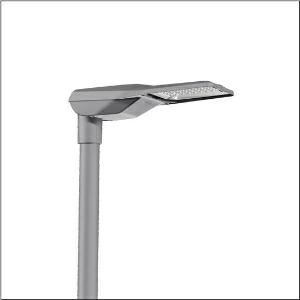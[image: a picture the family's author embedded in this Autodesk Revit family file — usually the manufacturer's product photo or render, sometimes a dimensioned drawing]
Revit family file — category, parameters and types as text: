
# Revit family: streetlight_sl_21_iq_mini___st0_8a_5xe2c41d08jb_a90a
name_source: partatom
category: Lighting Fixtures
units: mm (PartAtom-declared; Revit-internal decimal feet)

## family parameters
Cut with Voids When Loaded = No
Host = Face
Light Source = No
Part Type = Normal
Room Calculation Point = No
Round Connector Dimension = Use Diameter
Shared = No

## types (1)
- --- (1 x LED, 11290 lm, 71.6 W, 4000K)
    Apparent Load = 72 VA
    CIE Flux Codes = 41 75 97 100 100
    Color Rendering = 70
    Color Temperature = 4000K
    Default Elevation = 1800 mm
    Description = Streetlight SL 21 iQ mini, mast luminaire, primary light control with lens, of PMMA, primary optical cover: cover, of toughened safety glass, transparent, light distribution: ST0.8a, light emission: direct distribution, primary light characteristic: asymmetric, installation type: post-top, side-entry, LED, High Power LED, rated luminous flux: 11.290lm, luminous efficacy: 158lm/W, light colour: 740, colour temperature: 4000K, control: Auto-Match, Temp-Guard, Lumen-Switch, Night-Set, Smart-Wire, Light-Fading, Desk-Remote (wireless, voltage-free reading and setting of iQ features in the workshop via application-optimized NFC function/RFID function), optimised constant luminous flux control (CLO 2.0), presetting dimming linear, mains connection: 220..240V, AC, 50/60Hz, start of lifetime: 72W, end of service life: 75W, reduction: 33W, luminaire housing, of diecast aluminium, powder-coated, Siteco® metallic grey (DB 702S), corrosivity category C5 mid according to DIN EN ISO 12944, please order mast flange separately, inclination adjustable: 0°, 5°, 10°, 15°, sealing non-destructively replaceable, multi-level sealing system, length: 628mm, width: 235mm, height: 110mm, mast flange for spigot size: 42mm (side-entry): 5XC10008XM4, 60/48mm (side-entry/post-top): 5XC10108XM2, 76/60mm (side-entry/post-top): 5XC10108XM1, protection rating (complete): IP66, insulation class (complete): insulation class II (safety insulation), certification: CE, ENEC, ENEC+, VDE, impact resistance: IK09, permissible operating ambient temperature for outdoor applications: -40..+50°C, standard-compliant lighting for roads and squares, packaging unit: 1 piece

Light Distribution: ST0.8a
    Height = 110 mm
    Lamp = 1 x LED
    Lamp Light Flux = 11290 lm
    Lamp Power = 71.6 W
    Lamp count = 1
    Length = 625 mm
    Luminous efficacy = 158 lm/W
    Manufacturer = Siteco
    ModVariant = No
    Model = 5XE2C41D08JB
    Number of Poles = 1
    OnlyDefault = Yes
    Power Factor = 1
    Product Name = Streetlight SL 21 iQ mini | ST0.8a
    Product group = mast luminaire | pylon top
    ProductGroupID = 6100
    Protection Class = Protection class II
    Protection Degree = IP 66
    RLX_Detail_Level = 1
    RLX_Emergency_Light_Flux = 0 lm
    RLX_Emergency_Type = 0
    RLX_Emergency_Type_DB = No
    RlxData = <blob elided: 92389 chars, md5=4b9786a0>
    Socket = socket
    Standby Power = 0 W
    System Light Flux = 11290 lm
    System Power = 72 W
    Type Comments = factory setting: luminous flux: 100 % | dim-lin: 254 | 746 mA
    Type Image = l_1003519.jpg
    URL = http://relux.com
    VarID = @adj_101811
    Voltage = 0 V
    Weight = 0.00 kg
    Width = 234 mm

## geometry (parser evidence)
native form markers: Blend x4, Sweep x10
no freeform markers — native parametric forms only
